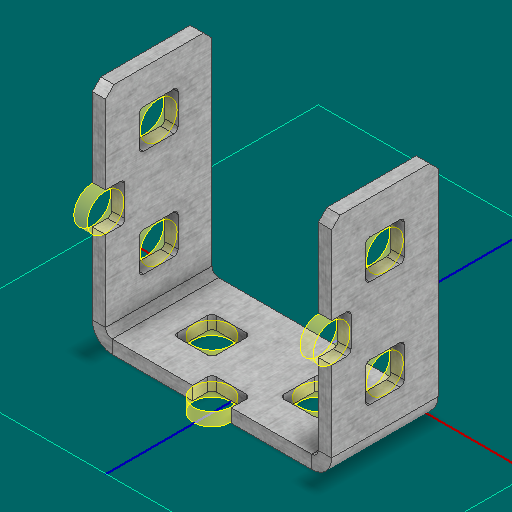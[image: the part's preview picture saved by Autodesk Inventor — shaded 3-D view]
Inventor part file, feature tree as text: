
AUTODESK INVENTOR PART (.ipt)
format: ipt  version: 2025 (Build 290162000, 162)  size: 475,648 bytes
history: native  units: in
note: dims shown in document units (in); Inventor stores cm internally (conversion verified against a paired STEP export)
features: other x173, sketch x2, sheet_metal_op x1
ambient origin geometry x8: Origin, YZ Plane, XZ Plane, XY Plane, X Axis, Y Axis, Z Axis, Center Point
bodies: Solid1 (feature_tree)
feature tree (176):
  other  "Alu C 2x2x2x1.ipt"
  other  "Solid1::Alu C 2x2x2x1.ipt"
  other  "TaggingFeature1"
  sketch  "Sketch1"  dims[d0=0.3937in]
  sketch  "Sketch2"  dims[d1=0.0625in]
  sheet_metal_op  "Body Pattern Sketch"
  other  "Arc Length"
  other  "Diagonal Plane"
  other  "Srf1"
  other  "Srf2"
  other  "Srf3"
  other  "Srf4"
  other  "Srf5"
  other  "Srf6"
  other  "Srf7"
  other  "Srf8"
  other  "Srf9"
  other  "Srf10"
  other  "Srf11"
  other  "Srf12"
  other  "Srf13"
  other  "Srf14"
  other  "Srf15"
  other  "Srf16"
  other  "Srf17"
  other  "Srf18"
  other  "Srf19"
  other  "Srf20"
  other  "Srf21"
  other  "Srf22"
  other  "Srf23"
  other  "Srf24"
  other  "Srf25"
  other  "Srf26"
  other  "Srf27"
  other  "Srf28"
  other  "Srf29"
  other  "Srf30"
  other  "Srf31"
  other  "Srf32"
  other  "Srf33"
  other  "Srf34"
  other  "Srf35"
  other  "Srf36"
  other  "Srf37"
  other  "Srf38"
  other  "Srf39"
  other  "Srf40"
  other  "Srf41"
  other  "Srf42"
  other  "Srf43"
  other  "Srf44"
  other  "Srf45"
  other  "Srf46"
  other  "Srf47"
  other  "Srf48"
  other  "Srf49"
  other  "Srf50"
  other  "Srf51"
  other  "Srf52"
  other  "Srf53"
  other  "Srf54"
  other  "Srf55"
  other  "Srf56"
  other  "Srf57"
  other  "Srf58"
  other  "Srf59"
  other  "Srf60"
  other  "Srf61"
  other  "Srf62"
  other  "Srf63"
  other  "Srf64"
  other  "Srf65"
  other  "Srf66"
  other  "Srf67"
  other  "Srf68"
  other  "Srf69"
  other  "Srf70"
  other  "Srf71"
  other  "Srf72"
  other  "Srf73"
  other  "Srf74"
  other  "Srf75"
  other  "Srf76"
  other  "Srf77"
  other  "Srf78"
  other  "Srf79"
  other  "Srf80"
  other  "Srf81"
  other  "Srf82"
  other  "Srf83"
  other  "Srf84"
  other  "Srf91::Derived"
  other  "Srf92::Derived"
  other  "Srf786::Derived"
  other  "Srf889::Derived"
  other  "Srf890::Derived"
  other  "Srf891::Derived"
  other  "Srf892::Derived"
  other  "Srf893::Derived"
  other  "Srf894::Derived"
  other  "Srf895::Derived"
  other  "Srf896::Derived"
  other  "Srf996::Derived"
  other  "Srf997::Derived"
  other  "Srf998::Derived"
  other  "Srf999::Derived"
  other  "Srf1000::Derived"
  other  "Srf1255::Derived"
  other  "Srf1256::Derived"
  other  "Srf1257::Derived"
  other  "Srf1258::Derived"
  other  "Srf1259::Derived"
  other  "Srf1315::Derived"
  other  "Srf1316::Derived"
  other  "Srf1317::Derived"
  other  "Srf1325::Derived"
  other  "Srf1326::Derived"
  other  "Srf1327::Derived"
  other  "Srf1328::Derived"
  other  "Srf1329::Derived"
  other  "Srf1330::Derived"
  other  "Srf1331::Derived"
  other  "Srf1332::Derived"
  other  "Srf1338::Derived"
  other  "Srf1339::Derived"
  other  "Srf1340::Derived"
  other  "Srf1341::Derived"
  other  "Srf1342::Derived"
  other  "Srf1369::Derived"
  other  "Srf1370::Derived"
  other  "Srf1371::Derived"
  other  "Srf1372::Derived"
  other  "Srf1373::Derived"
  other  "Srf1374::Derived"
  other  "Srf1375::Derived"
  other  "Srf1376::Derived"
  other  "Srf1384::Derived"
  other  "Srf1385::Derived"
  other  "Srf1386::Derived"
  other  "Srf1387::Derived"
  other  "Srf1388::Derived"
  other  "Srf1389::Derived"
  other  "Srf1390::Derived"
  other  "Srf1391::Derived"
  other  "Srf1397::Derived"
  other  "Srf1398::Derived"
  other  "Srf1399::Derived"
  other  "Srf1400::Derived"
  other  "Srf1401::Derived"
  other  "Srf1428::Derived"
  other  "Srf1429::Derived"
  other  "Srf1430::Derived"
  other  "Srf1431::Derived"
  other  "Srf1432::Derived"
  other  "Srf1433::Derived"
  other  "Srf1434::Derived"
  other  "Srf1473::Derived"
  other  "Srf1474::Derived"
  other  "Srf1475::Derived"
  other  "Srf1476::Derived"
  other  "Srf1477::Derived"
  other  "Srf1478::Derived"
  other  "Srf1479::Derived"
  other  "Srf1480::Derived"
  other  "Srf1481::Derived"
  other  "Srf1482::Derived"
  other  "Srf1483::Derived"
  other  "Srf1484::Derived"
  other  "Srf1485::Derived"
  other  "Srf1486::Derived"
  other  "Srf1487::Derived"
  other  "Srf1488::Derived"
  other  "Srf1489::Derived"
  other  "Srf1490::Derived"
  other  "Srf1491::Derived"
